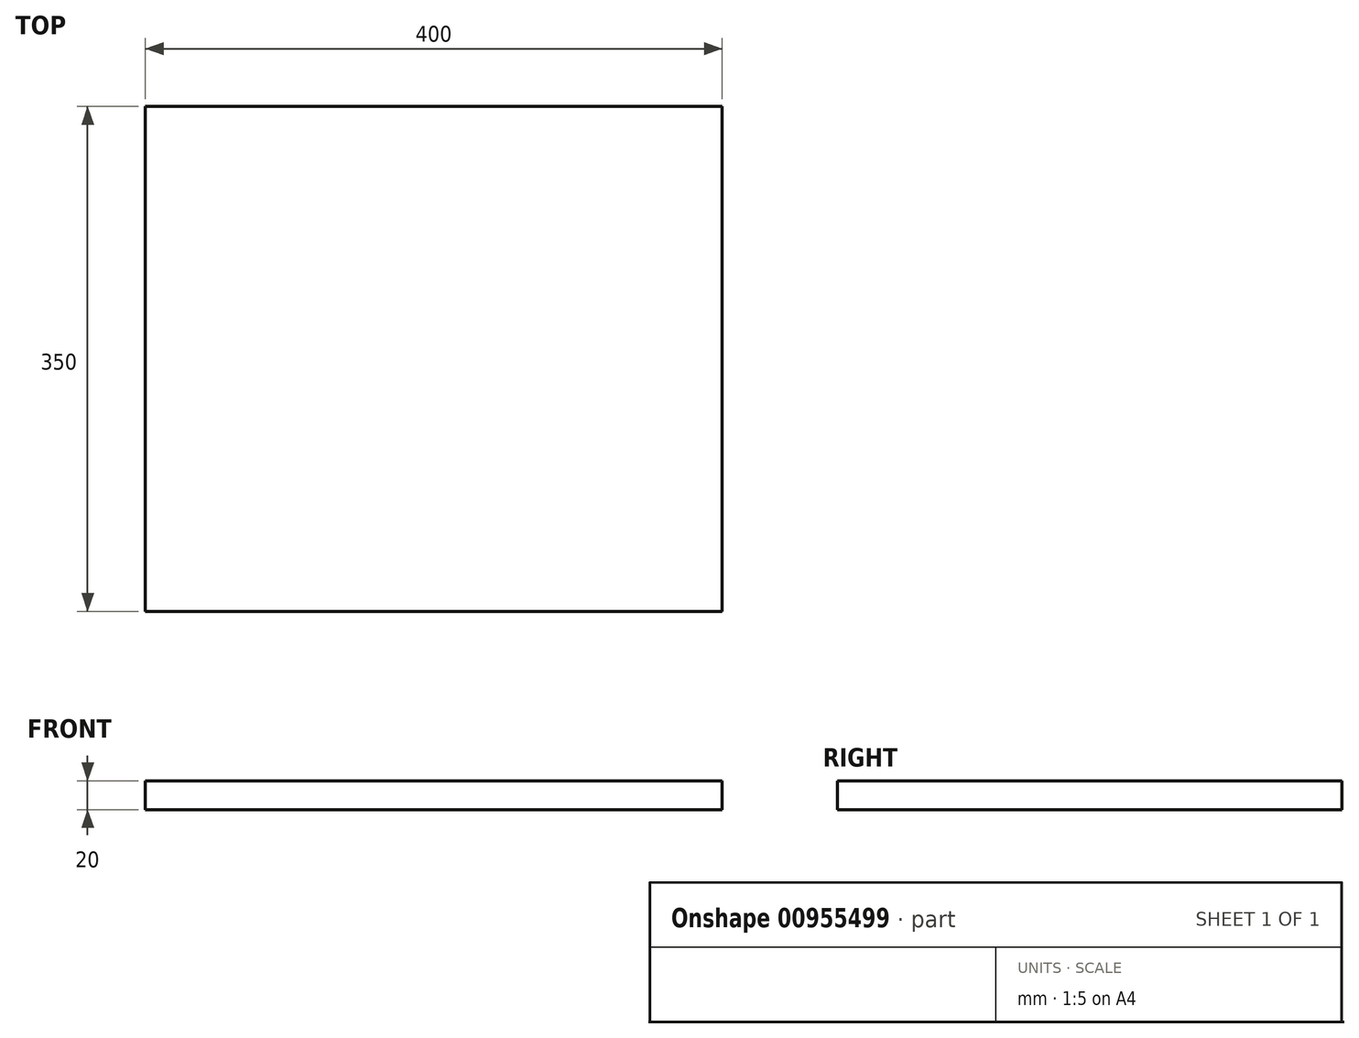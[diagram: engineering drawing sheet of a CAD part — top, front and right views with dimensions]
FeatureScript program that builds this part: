
annotation { "Feature Type Name" : "Feature", "Feature Type Description" : "" }
export const myFeature = defineFeature(function(context is Context, id is Id, definition is map)
    precondition{}
    {
        {
            var Q0;
            Q0=qCreatedBy(makeId("Top.planeOp"),FACE);
            var sketch = newSketch(context, id + "F0", { "sketchPlane" : qUnion([Q0])});
            skLineSegment(sketch, "E0", {"start": v(0, 0) * mm, "end": v(400, 0) * mm});
            skLineSegment(sketch, "E1", {"start": v(400, 0) * mm, "end": v(400, 350) * mm});
            skLineSegment(sketch, "E2", {"start": v(400, 350) * mm, "end": v(0, 350) * mm});
            skLineSegment(sketch, "E3", {"start": v(0, 350) * mm, "end": v(0, 0) * mm});
            skSolve(sketch);
        }
        {
            var Q0;
            Q0=makeQuery(id+"F0.imprint","IMPRINT",FACE,{"disambiguationData":[TD([[makeQuery(id+"F0.imprint","IMPRINT",EDGE,{"derivedFrom":sQuery(id+"F0.wireOp",EDGE,"E0")}),1.0]])]});
            extrude(context, id + "F1", {"entities" : qUnion([Q0]), "depth" : 20 * mm, "offsetDistance" : 25 * mm});
        }
    });
